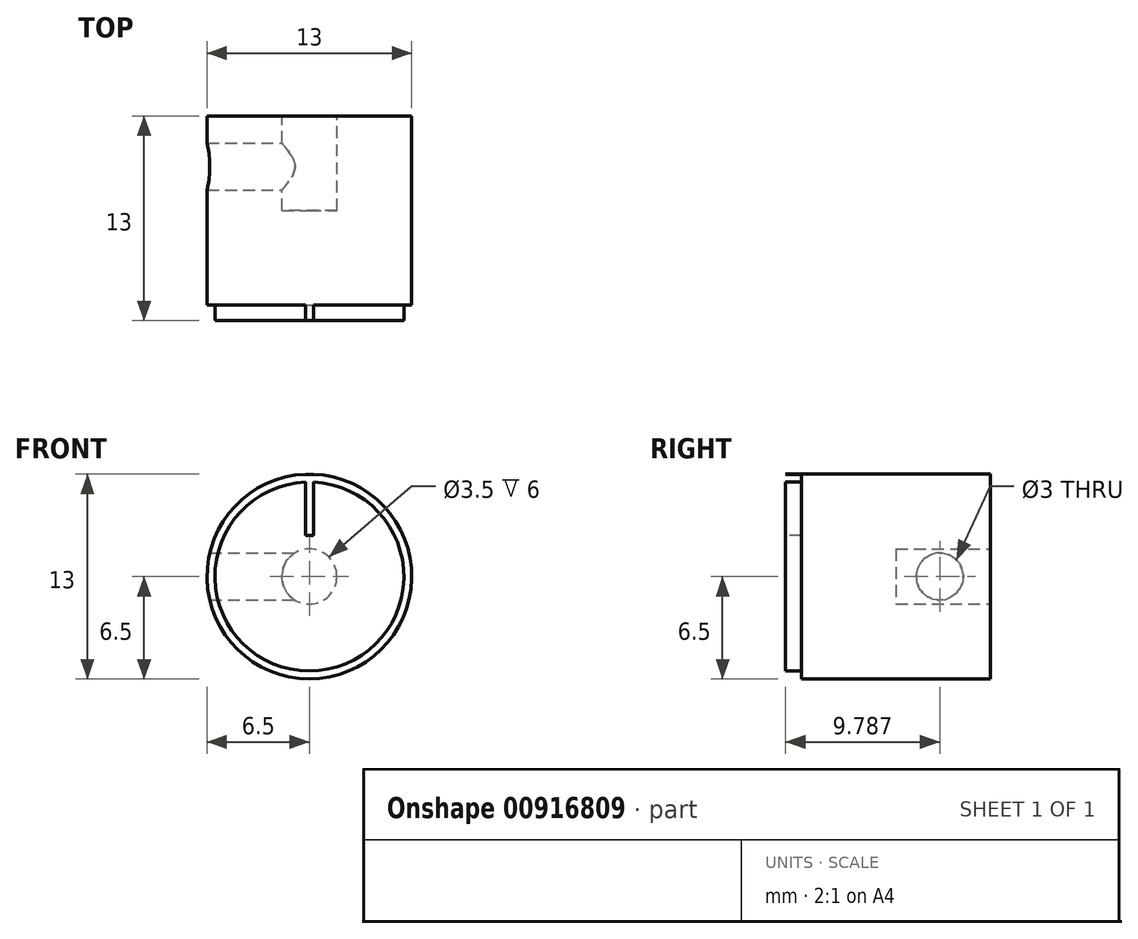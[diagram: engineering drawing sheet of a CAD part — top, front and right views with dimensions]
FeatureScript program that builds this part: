
annotation { "Feature Type Name" : "Feature", "Feature Type Description" : "" }
export const myFeature = defineFeature(function(context is Context, id is Id, definition is map)
    precondition{}
    {
        {
            var Q0;
            Q0=qCreatedBy(makeId("Front.planeOp"),FACE);
            var sketch = newSketch(context, id + "F0", { "sketchPlane" : qUnion([Q0])});
            skCircle(sketch, "E0", {"center": v(0, 0) * mm, "radius": 6.5 * mm});
            skSolve(sketch);
        }
        {
            var Q0;
            Q0=makeQuery(id+"F0.imprint","IMPRINT",FACE,{"disambiguationData":[TD([[makeQuery(id+"F0.imprint","IMPRINT",EDGE,{"derivedFrom":sQuery(id+"F0.wireOp",EDGE,"E0")}),1.0]])]});
            extrude(context, id + "F1", {"entities" : qUnion([Q0]), "depth" : 13 * mm, "offsetDistance" : 25 * mm});
        }
        {
            var Q0;
            Q0=makeQuery(id+"F1.opExtrude","CAP_FACE",FACE,{"disambiguationData":[OSD([sQuery(id+"F0.wireOp",EDGE,"E0")])],"isStart":false});
            var sketch = newSketch(context, id + "F2", { "sketchPlane" : qUnion([Q0])});
            skLineSegment(sketch, "E1.bottom", {"start": v(-0.25, 2.62) * mm, "end": v(0.25, 2.62) * mm});
            skPoint(sketch, "E1.middle", {"position": v(0, 0) * mm});
            skPoint(sketch, "E2.oppositeSnap0", {"position": v(0.25, 0) * mm});
            skLineSegment(sketch, "E2.top", {"start": v(-0.25, 6.5) * mm, "end": v(0.25, 6.5) * mm});
            skLineSegment(sketch, "E2.left", {"start": v(-0.25, 2.62) * mm, "end": v(-0.25, 6.5) * mm});
            skLineSegment(sketch, "E2.right", {"start": v(0.25, 2.62) * mm, "end": v(0.25, 6.5) * mm});
            skCircle(sketch, "E3", {"center": v(0, 0) * mm, "radius": 6 * mm});
            skSolve(sketch);
        }
        {
            var Q0;
            Q0=makeQuery(id+"F1.opExtrude","CAP_FACE",FACE,{"disambiguationData":[OSD([sQuery(id+"F0.wireOp",EDGE,"E0")])],"isStart":true});
            var sketch = newSketch(context, id + "F3", { "sketchPlane" : qUnion([Q0])});
            skCircle(sketch, "E4", {"center": v(0, 0) * mm, "radius": 1.75 * mm});
            skSolve(sketch);
        }
        {
            var Q0;
            {var subQ0=sQuery(id+"F2.wireOp",EDGE,"E1.bottom");Q0=makeQuery(id+"F2.imprint","IMPRINT",FACE,{"disambiguationData":[TD([[makeQuery(id+"F2.imprint","IMPRINT",EDGE,{"derivedFrom":subQ0}),1.0]])]});}
            var Q1;
            {var subQ0=sQuery(id+"F2.wireOp",EDGE,"E2.top");Q1=makeQuery(id+"F2.imprint","IMPRINT",FACE,{"disambiguationData":[TD([[makeQuery(id+"F2.imprint","IMPRINT",EDGE,{"derivedFrom":subQ0}),-1.0]])]});}
            var Q2;
            {var subQ0=sQuery(id+"F2.wireOp",EDGE,"E2.left");var subQ4=sQuery(id+"F2.wireOp",EDGE,"E3");var subQ5=makeQuery(id+"F2.imprint","INTERSECT",VERTEX,{"derivedFrom":[subQ0,subQ4]});Q2=makeQuery(id+"F2.imprint","IMPRINT",FACE,{"disambiguationData":[TD([[makeQuery(id+"F2.imprint","IMPRINT",EDGE,{"disambiguationData":[TD([[subQ5,-1.0]])],"derivedFrom":subQ4}),-1.0]])]});}
            extrude(context, id + "F4", {"entities" : qUnion([Q0, Q1, Q2]), "operationType" : NewBodyOperationType.REMOVE, "oppositeDirection" : true, "depth" : 1 * mm, "offsetDistance" : 25 * mm});
        }
        {
            var Q0;
            Q0=makeQuery(id+"F3.imprint","IMPRINT",FACE,{"disambiguationData":[TD([[makeQuery(id+"F3.imprint","IMPRINT",EDGE,{"derivedFrom":sQuery(id+"F3.wireOp",EDGE,"E4")}),1.0]])]});
            extrude(context, id + "F5", {"entities" : qUnion([Q0]), "operationType" : NewBodyOperationType.REMOVE, "oppositeDirection" : true, "depth" : 6 * mm, "offsetDistance" : 25 * mm});
        }
        {
            var Q0;
            Q0=qCreatedBy(makeId("Right.planeOp"),FACE);
            var sketch = newSketch(context, id + "F6", { "sketchPlane" : qUnion([Q0])});
            skCircle(sketch, "E5", {"center": v(-3.21, 0) * mm, "radius": 1.5 * mm});
            skSolve(sketch);
        }
        {
            var Q0;
            Q0=makeQuery(id+"F6.imprint","IMPRINT",FACE,{"disambiguationData":[TD([[makeQuery(id+"F6.imprint","IMPRINT",EDGE,{"derivedFrom":sQuery(id+"F6.wireOp",EDGE,"E5")}),1.0]])]});
            extrude(context, id + "F7", {"entities" : qUnion([Q0]), "operationType" : NewBodyOperationType.REMOVE, "oppositeDirection" : true, "depth" : 7 * mm, "offsetDistance" : 25 * mm});
        }
    });
